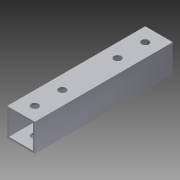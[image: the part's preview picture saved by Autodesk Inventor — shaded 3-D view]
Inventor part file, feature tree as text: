
AUTODESK INVENTOR PART (.ipt)
format: ipt  version: 2014 (Build 180170000, 170)  size: 100,864 bytes
history: native  units: in
note: dims shown in document units (in); Inventor stores cm internally (conversion verified against a paired STEP export)
features: extrude x2, sketch x2
ambient origin geometry x8: Origin, YZ Plane, XZ Plane, XY Plane, X Axis, Y Axis, Z Axis, Center Point
bodies: Solid1 (feature_tree)
feature tree (4):
  extrude  "Extrusion1"  Depth=1.0in
  extrude  "Extrusion2"  Depth=5.0in TaperAngle=0.0deg
  sketch  "Sketch1"  dims[d0=1.0in d1=1.0in]
  sketch  "Sketch2"  dims[d2=0.0625in d3=5.0in d4=0.0in d5=0.266in d6=0.5in d7=0.5in d8=0.7874in d10=1.0in d11=0.3937in d13=1.0in d15=4.0in d16=0.0in d17=0.5in d18=2.0in d19=0.7874in d21=1.0in d22=0.3937in d24=1.0in]
